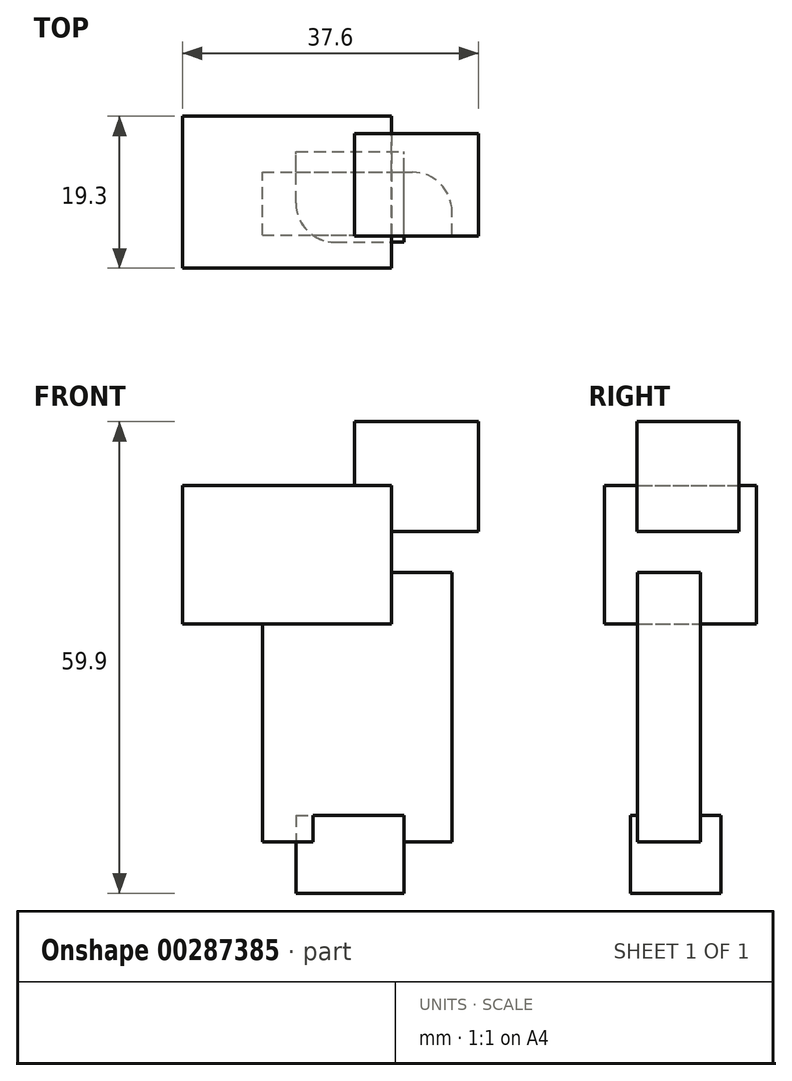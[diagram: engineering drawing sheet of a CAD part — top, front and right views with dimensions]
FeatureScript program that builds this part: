
annotation { "Feature Type Name" : "Feature", "Feature Type Description" : "" }
export const myFeature = defineFeature(function(context is Context, id is Id, definition is map)
    precondition{}
    {
        {
            var Q0;
            Q0=qCreatedBy(makeId("Front.planeOp"),FACE);
            var sketch = newSketch(context, id + "F0", { "sketchPlane" : qUnion([Q0])});
            skCircle(sketch, "E0", {"center": v(0, 0) * mm, "radius": 8.88 * mm, "construction": true});
            skLineSegment(sketch, "E1.bottom", {"start": v(-13.54, 21.6) * mm, "end": v(10.55, 21.6) * mm});
            skLineSegment(sketch, "E1.top", {"start": v(-13.54, -12.62) * mm, "end": v(10.55, -12.62) * mm});
            skLineSegment(sketch, "E1.left", {"start": v(-13.54, 21.6) * mm, "end": v(-13.54, -12.62) * mm});
            skLineSegment(sketch, "E1.right", {"start": v(10.55, 21.6) * mm, "end": v(10.55, -12.62) * mm});
            skLineSegment(sketch, "E2.bottom", {"start": v(-1.83, 40.75) * mm, "end": v(13.93, 40.75) * mm});
            skLineSegment(sketch, "E2.top", {"start": v(-1.83, 26.78) * mm, "end": v(13.93, 26.78) * mm});
            skLineSegment(sketch, "E2.left", {"start": v(-1.83, 40.75) * mm, "end": v(-1.83, 26.78) * mm});
            skLineSegment(sketch, "E2.right", {"start": v(13.93, 40.75) * mm, "end": v(13.93, 26.78) * mm});
            skLineSegment(sketch, "E3.bottom", {"start": v(-23.67, 32.64) * mm, "end": v(2.9, 32.64) * mm});
            skLineSegment(sketch, "E3.top", {"start": v(-23.67, 15.08) * mm, "end": v(2.9, 15.08) * mm});
            skLineSegment(sketch, "E3.left", {"start": v(-23.67, 32.64) * mm, "end": v(-23.67, 15.08) * mm});
            skLineSegment(sketch, "E3.right", {"start": v(2.9, 32.64) * mm, "end": v(2.9, 15.08) * mm});
            skLineSegment(sketch, "E4.bottom", {"start": v(-9.26, -9.24) * mm, "end": v(4.47, -9.24) * mm});
            skLineSegment(sketch, "E4.top", {"start": v(-9.26, -19.15) * mm, "end": v(4.47, -19.15) * mm});
            skLineSegment(sketch, "E4.left", {"start": v(-9.26, -9.24) * mm, "end": v(-9.26, -19.15) * mm});
            skLineSegment(sketch, "E4.right", {"start": v(4.47, -9.24) * mm, "end": v(4.47, -19.15) * mm});
            skSolve(sketch);
        }
        {
            var Q0;
            {var subQ0=sQuery(id+"F0.wireOp",EDGE,"E1.right");Q0=makeQuery(id+"F0.imprint","IMPRINT",FACE,{"disambiguationData":[TD([[makeQuery(id+"F0.imprint","IMPRINT",EDGE,{"derivedFrom":subQ0}),-1.0]])]});}
            extrude(context, id + "F1", {"entities" : qUnion([Q0]), "depth" : 4 * mm, "hasSecondDirection" : true, "secondDirectionOppositeDirection" : true, "secondDirectionDepth" : 4 * mm});
        }
        {
            var Q0;
            {var subQ0=sQuery(id+"F0.wireOp",EDGE,"E1.left");var subQ1=sQuery(id+"F0.wireOp",EDGE,"E1.bottom");var subQ2=makeQuery(id+"F0.imprint","INTERSECT",VERTEX,{"derivedFrom":[subQ1,subQ0]});Q0=makeQuery(id+"F0.imprint","IMPRINT",FACE,{"disambiguationData":[TD([[makeQuery(id+"F0.imprint","IMPRINT",EDGE,{"disambiguationData":[TD([[subQ2,-1.0]])],"derivedFrom":subQ1}),-1.0]])]});}
            var Q1;
            {var subQ13=sQuery(id+"F0.wireOp",EDGE,"E3.left");Q1=makeQuery(id+"F0.imprint","IMPRINT",FACE,{"disambiguationData":[TD([[makeQuery(id+"F0.imprint","IMPRINT",EDGE,{"derivedFrom":subQ13}),1.0]])]});}
            var Q2;
            {var subQ0=sQuery(id+"F0.wireOp",EDGE,"E2.left");var subQ1=sQuery(id+"F0.wireOp",EDGE,"E2.top");var subQ2=makeQuery(id+"F0.imprint","INTERSECT",VERTEX,{"derivedFrom":[subQ1,subQ0]});Q2=makeQuery(id+"F0.imprint","IMPRINT",FACE,{"disambiguationData":[TD([[makeQuery(id+"F0.imprint","IMPRINT",EDGE,{"disambiguationData":[TD([[subQ2,-1.0]])],"derivedFrom":subQ1}),1.0]])]});}
            extrude(context, id + "F2", {"entities" : qUnion([Q0, Q1, Q2]), "operationType" : NewBodyOperationType.ADD, "depth" : 8.2 * mm, "hasSecondDirection" : true, "secondDirectionOppositeDirection" : true, "secondDirectionDepth" : 11.1 * mm});
        }
        {
            var Q0;
            {var subQ1=sQuery(id+"F0.wireOp",EDGE,"E2.bottom");Q0=makeQuery(id+"F0.imprint","IMPRINT",FACE,{"disambiguationData":[TD([[makeQuery(id+"F0.imprint","IMPRINT",EDGE,{"derivedFrom":subQ1}),-1.0]])]});}
            var Q1;
            {var subQ0=sQuery(id+"F0.wireOp",EDGE,"E2.left");var subQ1=sQuery(id+"F0.wireOp",EDGE,"E2.top");var subQ2=makeQuery(id+"F0.imprint","INTERSECT",VERTEX,{"derivedFrom":[subQ1,subQ0]});Q1=makeQuery(id+"F0.imprint","IMPRINT",FACE,{"disambiguationData":[TD([[makeQuery(id+"F0.imprint","IMPRINT",EDGE,{"disambiguationData":[TD([[subQ2,-1.0]])],"derivedFrom":subQ1}),1.0]])]});}
            extrude(context, id + "F3", {"entities" : qUnion([Q0, Q1]), "operationType" : NewBodyOperationType.ADD, "depth" : 4.1 * mm, "hasSecondDirection" : true, "secondDirectionOppositeDirection" : true, "secondDirectionDepth" : 8.9 * mm});
        }
        {
            var Q0;
            {var subQ5=sQuery(id+"F0.wireOp",EDGE,"E4.bottom");Q0=makeQuery(id+"F0.imprint","IMPRINT",FACE,{"disambiguationData":[TD([[makeQuery(id+"F0.imprint","IMPRINT",EDGE,{"derivedFrom":subQ5}),-1.0]])]});}
            var Q1;
            {var subQ5=sQuery(id+"F0.wireOp",EDGE,"E4.top");Q1=makeQuery(id+"F0.imprint","IMPRINT",FACE,{"disambiguationData":[TD([[makeQuery(id+"F0.imprint","IMPRINT",EDGE,{"derivedFrom":subQ5}),1.0]])]});}
            extrude(context, id + "F4", {"entities" : qUnion([Q0, Q1]), "operationType" : NewBodyOperationType.ADD, "depth" : 4.9 * mm, "hasSecondDirection" : true, "secondDirectionOppositeDirection" : true, "secondDirectionDepth" : 6.6 * mm});
        }
        {
            var Q0;
            Q0=makeQuery(id+"F1.opExtrude","CAP_EDGE",EDGE,{"disambiguationData":[OSD([sQuery(id+"F0.wireOp",EDGE,"E1.right")])],"isStart":true});
            var Q1;
            Q1=makeQuery(id+"F4.opExtrude","CAP_EDGE",EDGE,{"disambiguationData":[OSD([sQuery(id+"F0.wireOp",EDGE,"E4.left")])],"isStart":false});
            fillet(context, id + "F5", {"entities" : qUnion([Q0, Q1]), "radius" : 5 * mm, "tangentPropagation" : true, "allowEdgeOverflow" : false});
        }
    });
